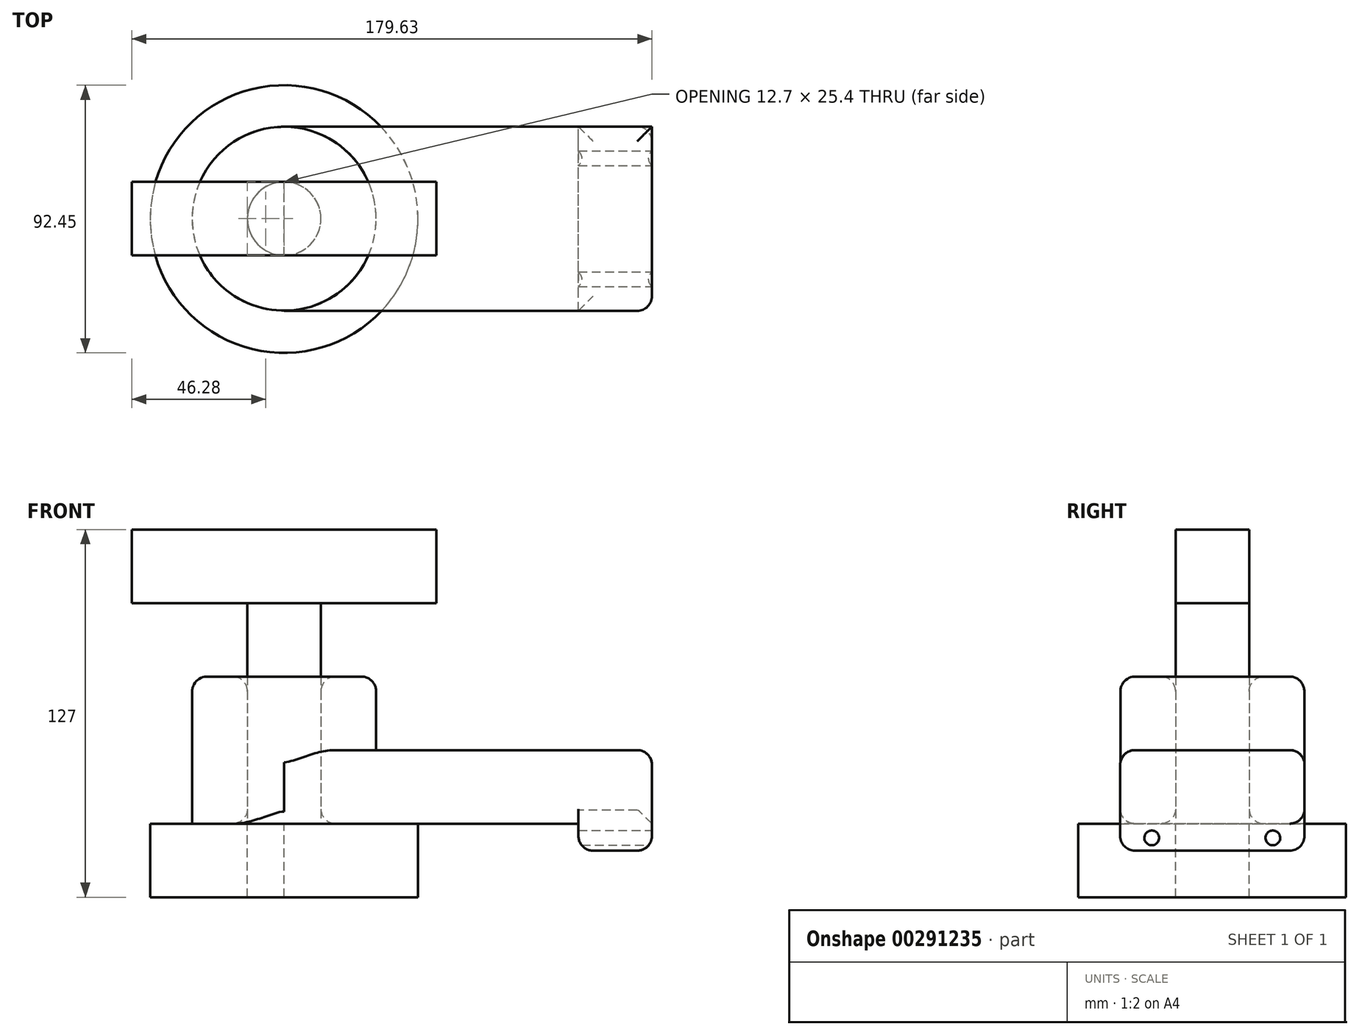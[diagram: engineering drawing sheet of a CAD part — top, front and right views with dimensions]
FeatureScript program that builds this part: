
annotation { "Feature Type Name" : "Feature", "Feature Type Description" : "" }
export const myFeature = defineFeature(function(context is Context, id is Id, definition is map)
    precondition{}
    {
        {
            var Q0;
            Q0=qCreatedBy(makeId("Top.planeOp"),FACE);
            var sketch = newSketch(context, id + "F0", { "sketchPlane" : qUnion([Q0])});
            skLineSegment(sketch, "E0.bottom", {"start": v(0, 0) * mm, "end": v(127, 0) * mm});
            skLineSegment(sketch, "E0.top", {"start": v(0, 63.66) * mm, "end": v(127, 63.66) * mm});
            skLineSegment(sketch, "E0.left", {"start": v(0, 0) * mm, "end": v(0, 63.66) * mm});
            skLineSegment(sketch, "E0.right", {"start": v(127, 0) * mm, "end": v(127, 63.66) * mm});
            skCircle(sketch, "E1", {"center": v(0, 31.83) * mm, "radius": 31.75 * mm});
            skCircle(sketch, "E2", {"center": v(0, 31.83) * mm, "radius": 12.7 * mm});
            skSolve(sketch);
        }
        {
            var Q0;
            {var subQ0=sQuery(id+"F0.wireOp",EDGE,"E1");var subQ1=sQuery(id+"F0.wireOp",EDGE,"E0.left");var subQ2=makeQuery(id+"F0.imprint","INTERSECT",VERTEX,{"disambiguationData":[OD(0.0)],"derivedFrom":[subQ1,subQ0]});Q0=makeQuery(id+"F0.imprint","IMPRINT",FACE,{"disambiguationData":[TD([[makeQuery(id+"F0.imprint","IMPRINT",EDGE,{"disambiguationData":[TD([[subQ2,-1.0]])],"derivedFrom":subQ1}),1.0]])]});}
            var Q1;
            {var subQ0=sQuery(id+"F0.wireOp",EDGE,"E1");var subQ1=sQuery(id+"F0.wireOp",EDGE,"E0.left");var subQ2=makeQuery(id+"F0.imprint","INTERSECT",VERTEX,{"disambiguationData":[OD(0.0)],"derivedFrom":[subQ1,subQ0]});Q1=makeQuery(id+"F0.imprint","IMPRINT",FACE,{"disambiguationData":[TD([[makeQuery(id+"F0.imprint","IMPRINT",EDGE,{"disambiguationData":[TD([[subQ2,-1.0]])],"derivedFrom":subQ1}),-1.0]])]});}
            var Q2;
            {var subQ1=sQuery(id+"F0.wireOp",EDGE,"E0.bottom");Q2=makeQuery(id+"F0.imprint","IMPRINT",FACE,{"disambiguationData":[TD([[makeQuery(id+"F0.imprint","IMPRINT",EDGE,{"derivedFrom":subQ1}),1.0]])]});}
            extrude(context, id + "F1", {"entities" : qUnion([Q0, Q1, Q2]), "depth" : 25.4 * mm});
        }
        {
            var Q0;
            Q0 = qSketchRegion(id + "F0", true);
            extrude(context, id + "F2", {"entities" : qUnion([Q0]), "operationType" : NewBodyOperationType.ADD, "depth" : 25.4 * mm});
        }
        {
            var Q0;
            {var subQ0=sQuery(id+"F0.wireOp",EDGE,"E1");var subQ1=sQuery(id+"F0.wireOp",EDGE,"E0.left");var subQ2=makeQuery(id+"F0.imprint","INTERSECT",VERTEX,{"disambiguationData":[OD(0.0)],"derivedFrom":[subQ1,subQ0]});Q0=makeQuery(id+"F0.imprint","IMPRINT",FACE,{"disambiguationData":[TD([[makeQuery(id+"F0.imprint","IMPRINT",EDGE,{"disambiguationData":[TD([[subQ2,-1.0]])],"derivedFrom":subQ1}),1.0]])]});}
            var Q1;
            {var subQ0=sQuery(id+"F0.wireOp",EDGE,"E1");var subQ1=sQuery(id+"F0.wireOp",EDGE,"E0.left");var subQ2=makeQuery(id+"F0.imprint","INTERSECT",VERTEX,{"disambiguationData":[OD(0.0)],"derivedFrom":[subQ1,subQ0]});Q1=makeQuery(id+"F0.imprint","IMPRINT",FACE,{"disambiguationData":[TD([[makeQuery(id+"F0.imprint","IMPRINT",EDGE,{"disambiguationData":[TD([[subQ2,-1.0]])],"derivedFrom":subQ1}),-1.0]])]});}
            extrude(context, id + "F3", {"entities" : qUnion([Q0, Q1]), "operationType" : NewBodyOperationType.ADD, "depth" : 50.8 * mm});
        }
        {
            var Q0;
            Q0=makeQuery(id+"F1.opExtrude","SWEPT_FACE",FACE,{"disambiguationData":[OSD([sQuery(id+"F0.wireOp",EDGE,"E0.right")])]});
            var sketch = newSketch(context, id + "F4", { "sketchPlane" : qUnion([Q0])});
            skLineSegment(sketch, "E3.bottom", {"start": v(0, 25.4) * mm, "end": v(63.64, 25.4) * mm});
            skLineSegment(sketch, "E3.top", {"start": v(0, -9.33) * mm, "end": v(63.64, -9.33) * mm});
            skLineSegment(sketch, "E3.left", {"start": v(0, 25.4) * mm, "end": v(0, -9.33) * mm});
            skLineSegment(sketch, "E3.right", {"start": v(63.64, 25.4) * mm, "end": v(63.64, -9.33) * mm});
            skSolve(sketch);
        }
        {
            var Q0;
            {var subQ0=sQuery(id+"F4.wireOp",EDGE,"E3.top");Q0=makeQuery(id+"F4.imprint","IMPRINT",FACE,{"disambiguationData":[TD([[makeQuery(id+"F4.imprint","IMPRINT",EDGE,{"derivedFrom":subQ0}),1.0]])]});}
            var sketch = newSketch(context, id + "F5", { "sketchPlane" : qUnion([Q0])});
            skLineSegment(sketch, "E4", {"start": v(31.8, 0) * mm, "end": v(31.8, -9.38) * mm, "construction": true});
            skCircle(sketch, "E5", {"center": v(10.9, -4.91) * mm, "radius": 2.54 * mm});
            skCircle(sketch, "E6.MirrorC", {"center": v(52.7, -4.91) * mm, "radius": 2.54 * mm});
            skSolve(sketch);
        }
        {
            var Q0;
            Q0=makeQuery(id+"F5.imprint","IMPRINT",FACE,{"disambiguationData":[TD([[makeQuery(id+"F5.imprint","IMPRINT",EDGE,{"derivedFrom":sQuery(id+"F5.wireOp",EDGE,"E5")}),-1.0]])]});
            extrude(context, id + "F6", {"entities" : qUnion([Q0]), "operationType" : NewBodyOperationType.ADD, "oppositeDirection" : true, "depth" : 25.4 * mm});
        }
        {
            var Q0;
            Q0=makeQuery(id+"F1.opExtrude","CAP_EDGE",EDGE,{"disambiguationData":[OSD([sQuery(id+"F0.wireOp",EDGE,"E0.bottom")])],"isStart":false});
            var Q1;
            Q1=makeQuery(id+"F1.opExtrude","CAP_EDGE",EDGE,{"disambiguationData":[OSD([sQuery(id+"F0.wireOp",EDGE,"E0.top")])],"isStart":false});
            var Q2;
            Q2=makeQuery(id+"F1.opExtrude","CAP_EDGE",EDGE,{"disambiguationData":[OSD([sQuery(id+"F0.wireOp",EDGE,"E0.right")])],"isStart":false});
            var Q3;
            Q3=makeQuery(id+"F1.opExtrude","CAP_EDGE",EDGE,{"disambiguationData":[OSD([sQuery(id+"F0.wireOp",EDGE,"E0.top")])],"isStart":true});
            var Q4;
            Q4=makeQuery(id+"F6.opExtrude","CAP_EDGE",EDGE,{"disambiguationData":[OSD([sQuery(id+"F4.wireOp",EDGE,"E3.top")])],"isStart":false});
            var Q5;
            Q5=makeQuery(id+"F1.opExtrude","CAP_EDGE",EDGE,{"disambiguationData":[OSD([sQuery(id+"F0.wireOp",EDGE,"E0.bottom")])],"isStart":true});
            var Q6;
            Q6=makeQuery(id+"F6.opExtrude","SWEPT_EDGE",EDGE,{"disambiguationData":[OSD([sQuery(id+"F4.wireOp",EDGE,"E3.top"),sQuery(id+"F4.wireOp",EDGE,"E3.left")])]});
            var Q7;
            Q7=makeQuery(id+"F6.opExtrude","SWEPT_EDGE",EDGE,{"disambiguationData":[OSD([sQuery(id+"F4.wireOp",EDGE,"E3.top"),sQuery(id+"F4.wireOp",EDGE,"E3.right")])]});
            var Q8;
            Q8=makeQuery(id+"F1.opExtrude","CAP_EDGE",EDGE,{"disambiguationData":[OSD([sQuery(id+"F0.wireOp",EDGE,"E2")])],"isStart":true});
            var Q9;
            Q9=makeQuery(id+"F3.opExtrude","CAP_EDGE",EDGE,{"disambiguationData":[OSD([sQuery(id+"F0.wireOp",EDGE,"E2")])],"isStart":false});
            var Q10;
            Q10=makeQuery(id+"F3.opExtrude","CAP_EDGE",EDGE,{"disambiguationData":[OSD([sQuery(id+"F0.wireOp",EDGE,"E1")])],"isStart":false});
            var Q11;
            {var subQ0=sQuery(id+"F0.wireOp",EDGE,"E2");Q11=makeQuery(id+"F3.boolean.opBoolean","MERGE",FACE,{"derivedFrom":[makeQuery(id+"F1.opExtrude","SWEPT_FACE",FACE,{"disambiguationData":[OSD([subQ0])]}),makeQuery(id+"F3.opExtrude","SWEPT_FACE",FACE,{"disambiguationData":[OSD([subQ0])]})]});}
            fillet(context, id + "F7", {"entities" : qUnion([Q0, Q1, Q2, Q3, Q4, Q5, Q6, Q7, Q8, Q9, Q10, Q11]), "radius" : 5.08 * mm, "tangentPropagation" : true, "allowEdgeOverflow" : false});
        }
        {
            var Q0;
            Q0=makeQuery(id+"F6.opExtrude","CAP_EDGE",EDGE,{"disambiguationData":[OSD([sQuery(id+"F4.wireOp",EDGE,"E3.top")])],"isStart":true});
            fillet(context, id + "F8", {"entities" : qUnion([Q0]), "radius" : 5.08 * mm, "tangentPropagation" : true, "allowEdgeOverflow" : false});
        }
        {
            var Q0;
            {var subQ0=sQuery(id+"F0.wireOp",EDGE,"E2");var subQ1=sQuery(id+"F0.wireOp",EDGE,"E0.left");var subQ2=makeQuery(id+"F0.imprint","INTERSECT",VERTEX,{"disambiguationData":[OD(0.0)],"derivedFrom":[subQ1,subQ0]});Q0=makeQuery(id+"F0.imprint","IMPRINT",FACE,{"disambiguationData":[TD([[makeQuery(id+"F0.imprint","IMPRINT",EDGE,{"disambiguationData":[TD([[subQ2,-1.0]])],"derivedFrom":subQ1}),-1.0]])]});}
            var Q1;
            {var subQ0=sQuery(id+"F0.wireOp",EDGE,"E2");var subQ1=sQuery(id+"F0.wireOp",EDGE,"E0.left");var subQ2=makeQuery(id+"F0.imprint","INTERSECT",VERTEX,{"disambiguationData":[OD(0.0)],"derivedFrom":[subQ1,subQ0]});Q1=makeQuery(id+"F0.imprint","IMPRINT",FACE,{"disambiguationData":[TD([[makeQuery(id+"F0.imprint","IMPRINT",EDGE,{"disambiguationData":[TD([[subQ2,-1.0]])],"derivedFrom":subQ1}),1.0]])]});}
            extrude(context, id + "F9", {"entities" : qUnion([Q0, Q1]), "depth" : 76.2 * mm});
        }
        {
            var Q0;
            Q0=makeQuery(id+"F9.opExtrude","CAP_FACE",FACE,{"disambiguationData":[OSD([sQuery(id+"F0.wireOp",EDGE,"E2")])],"isStart":false});
            var sketch = newSketch(context, id + "F10", { "sketchPlane" : qUnion([Q0])});
            skLineSegment(sketch, "E7.bottom", {"start": v(52.63, 19.14) * mm, "end": v(-52.63, 19.14) * mm});
            skLineSegment(sketch, "E7.top", {"start": v(52.63, 44.52) * mm, "end": v(-52.63, 44.52) * mm});
            skLineSegment(sketch, "E7.left", {"start": v(52.63, 19.14) * mm, "end": v(52.63, 44.52) * mm});
            skLineSegment(sketch, "E7.right", {"start": v(-52.63, 19.14) * mm, "end": v(-52.63, 44.52) * mm});
            skPoint(sketch, "E7.middle", {"position": v(0, 31.83) * mm});
            skSolve(sketch);
        }
        {
            var Q0;
            Q0 = qSketchRegion(id + "F10", true);
            extrude(context, id + "F11", {"entities" : qUnion([Q0]), "operationType" : NewBodyOperationType.ADD, "depth" : 25.4 * mm});
        }
        {
            var Q0;
            {var subQ0=sQuery(id+"F0.wireOp",EDGE,"E2");var subQ1=sQuery(id+"F0.wireOp",EDGE,"E0.left");var subQ2=makeQuery(id+"F0.imprint","INTERSECT",VERTEX,{"disambiguationData":[OD(0.0)],"derivedFrom":[subQ1,subQ0]});Q0=makeQuery(id+"F0.imprint","IMPRINT",FACE,{"disambiguationData":[TD([[makeQuery(id+"F0.imprint","IMPRINT",EDGE,{"disambiguationData":[TD([[subQ2,-1.0]])],"derivedFrom":subQ1}),1.0]])]});}
            var sketch = newSketch(context, id + "F12", { "sketchPlane" : qUnion([Q0])});
            skCircle(sketch, "E8", {"center": v(0, 31.7) * mm, "radius": 46.23 * mm});
            skSolve(sketch);
        }
        {
            var Q0;
            Q0=makeQuery(id+"F12.imprint","IMPRINT",FACE,{"disambiguationData":[TD([[makeQuery(id+"F12.imprint","IMPRINT",EDGE,{"derivedFrom":sQuery(id+"F12.wireOp",EDGE,"E8")}),1.0]])]});
            extrude(context, id + "F13", {"entities" : qUnion([Q0]), "oppositeDirection" : true, "depth" : 25.4 * mm});
        }
    });
